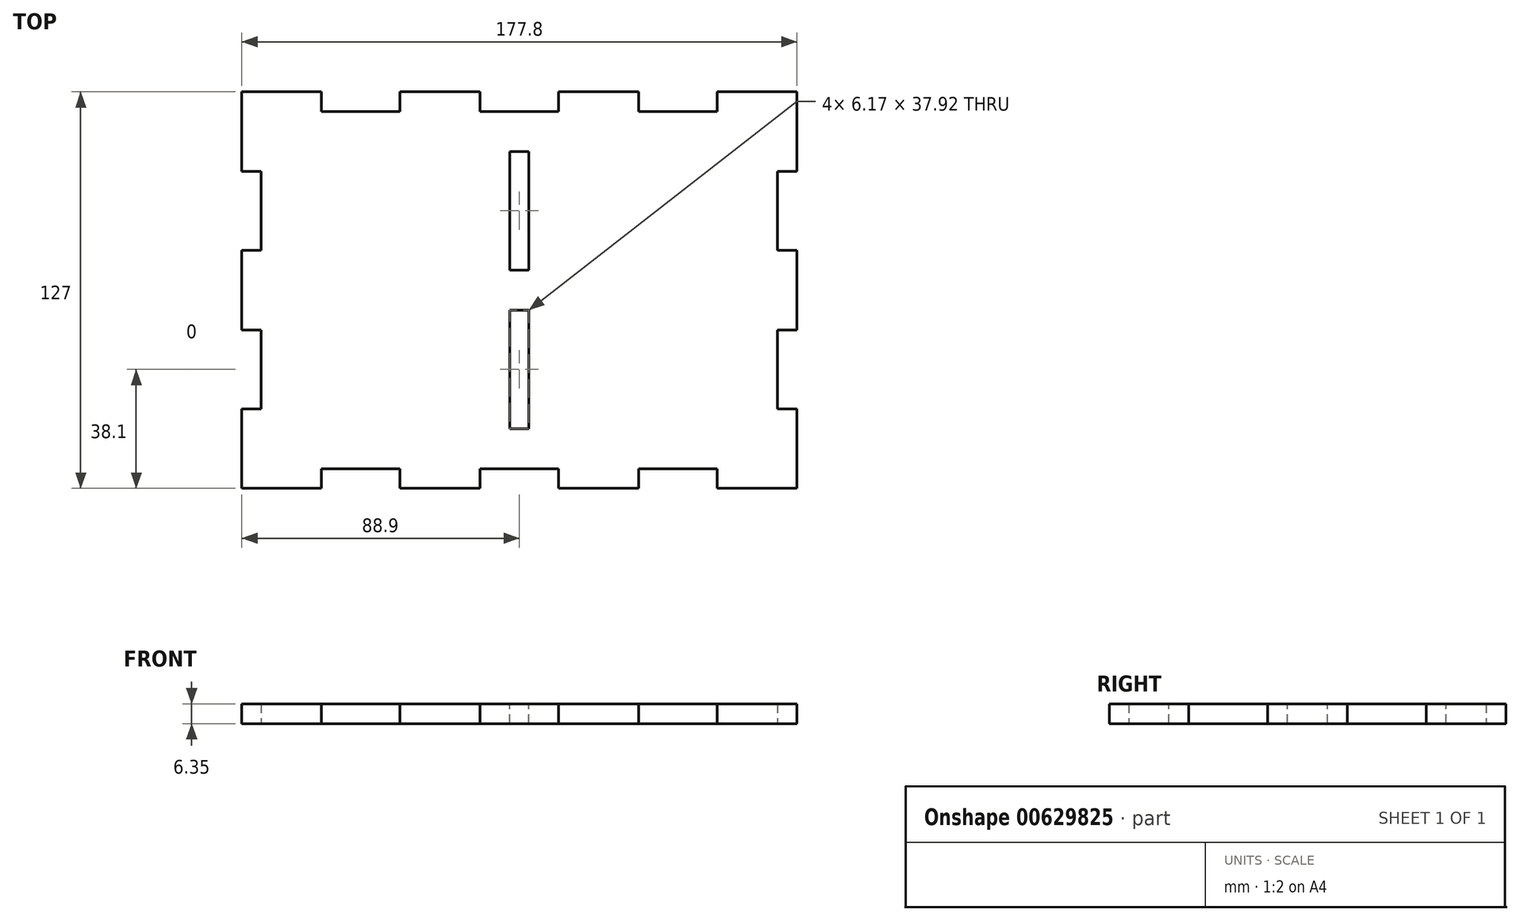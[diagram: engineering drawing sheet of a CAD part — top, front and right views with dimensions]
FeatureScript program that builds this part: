
annotation { "Feature Type Name" : "Feature", "Feature Type Description" : "" }
export const myFeature = defineFeature(function(context is Context, id is Id, definition is map)
    precondition{}
    {
        {
            var Q0;
            Q0=qCreatedBy(makeId("Top.planeOp"),FACE);
            var sketch = newSketch(context, id + "F0", { "sketchPlane" : qUnion([Q0])});
            skLineSegment(sketch, "E0.bottom", {"start": v(0, 0) * mm, "end": v(177.8, 0) * mm});
            skLineSegment(sketch, "E0.top", {"start": v(0, 127) * mm, "end": v(177.8, 127) * mm});
            skLineSegment(sketch, "E0.left", {"start": v(0, 0) * mm, "end": v(0, 127) * mm});
            skLineSegment(sketch, "E0.right", {"start": v(177.8, 0) * mm, "end": v(177.8, 127) * mm});
            skLineSegment(sketch, "E1.top", {"start": v(25.49, 6.26) * mm, "end": v(50.71, 6.26) * mm});
            skLineSegment(sketch, "E1.left", {"start": v(25.49, 0) * mm, "end": v(25.49, 6.26) * mm});
            skLineSegment(sketch, "E1.right", {"start": v(50.71, 0) * mm, "end": v(50.71, 6.26) * mm});
            skPoint(sketch, "E2", {"position": v(38.1, 6.26) * mm});
            skLineSegment(sketch, "E3.bottom", {"start": v(76.29, 0) * mm, "end": v(101.51, 0) * mm});
            skLineSegment(sketch, "E3.top", {"start": v(76.29, 6.26) * mm, "end": v(101.51, 6.26) * mm});
            skLineSegment(sketch, "E3.left", {"start": v(76.29, 0) * mm, "end": v(76.29, 6.26) * mm});
            skLineSegment(sketch, "E3.right", {"start": v(101.51, 0) * mm, "end": v(101.51, 6.26) * mm});
            skPoint(sketch, "E4", {"position": v(88.9, 6.26) * mm});
            skLineSegment(sketch, "E5.bottom", {"start": v(127.09, 0) * mm, "end": v(152.31, 0) * mm});
            skLineSegment(sketch, "E5.top", {"start": v(127.09, 6.26) * mm, "end": v(152.31, 6.26) * mm});
            skLineSegment(sketch, "E5.left", {"start": v(127.09, 0) * mm, "end": v(127.09, 6.26) * mm});
            skLineSegment(sketch, "E5.right", {"start": v(152.31, 0) * mm, "end": v(152.31, 6.26) * mm});
            skPoint(sketch, "E6", {"position": v(139.7, 6.26) * mm});
            skLineSegment(sketch, "E7.bottom", {"start": v(177.8, 25.49) * mm, "end": v(171.54, 25.49) * mm});
            skLineSegment(sketch, "E7.top", {"start": v(177.8, 50.71) * mm, "end": v(171.54, 50.71) * mm});
            skLineSegment(sketch, "E7.left", {"start": v(177.8, 25.49) * mm, "end": v(177.8, 50.71) * mm});
            skLineSegment(sketch, "E7.right", {"start": v(171.54, 25.49) * mm, "end": v(171.54, 50.71) * mm});
            skPoint(sketch, "E8", {"position": v(171.54, 38.1) * mm});
            skPoint(sketch, "E9", {"position": v(0, 63.5) * mm});
            skPoint(sketch, "E10", {"position": v(177.8, 63.5) * mm});
            skLineSegment(sketch, "E11", {"start": v(0, 63.5) * mm, "end": v(177.8, 63.5) * mm, "construction": true});
            skLineSegment(sketch, "E12.MirrorCS", {"start": v(25.49, 120.74) * mm, "end": v(50.71, 120.74) * mm});
            skLineSegment(sketch, "E13.MirrorCS", {"start": v(127.09, 120.74) * mm, "end": v(152.31, 120.74) * mm});
            skLineSegment(sketch, "E14.MirrorCS", {"start": v(50.71, 127) * mm, "end": v(50.71, 120.74) * mm});
            skLineSegment(sketch, "E15.MirrorCS", {"start": v(101.51, 127) * mm, "end": v(101.51, 120.74) * mm});
            skLineSegment(sketch, "E16.MirrorCS", {"start": v(76.29, 127) * mm, "end": v(101.51, 127) * mm});
            skPoint(sketch, "E17.MirrorP", {"position": v(139.7, 120.74) * mm});
            skLineSegment(sketch, "E18.MirrorCS", {"start": v(152.31, 127) * mm, "end": v(152.31, 120.74) * mm});
            skLineSegment(sketch, "E19.MirrorCS", {"start": v(127.09, 127) * mm, "end": v(152.31, 127) * mm});
            skLineSegment(sketch, "E20.MirrorCS", {"start": v(25.49, 127) * mm, "end": v(25.49, 120.74) * mm});
            skPoint(sketch, "E21.MirrorP", {"position": v(88.9, 120.74) * mm});
            skLineSegment(sketch, "E22.MirrorCS", {"start": v(127.09, 127) * mm, "end": v(127.09, 120.74) * mm});
            skLineSegment(sketch, "E23.MirrorCS", {"start": v(76.29, 120.74) * mm, "end": v(101.51, 120.74) * mm});
            skLineSegment(sketch, "E24.MirrorCS", {"start": v(76.29, 127) * mm, "end": v(76.29, 120.74) * mm});
            skPoint(sketch, "E25.MirrorP", {"position": v(38.1, 120.74) * mm});
            skLineSegment(sketch, "E26.MirrorCS", {"start": v(171.54, 101.51) * mm, "end": v(171.54, 76.29) * mm});
            skLineSegment(sketch, "E27.MirrorCS", {"start": v(177.8, 101.51) * mm, "end": v(177.8, 76.29) * mm});
            skLineSegment(sketch, "E28.MirrorCS", {"start": v(177.8, 101.51) * mm, "end": v(171.54, 101.51) * mm});
            skLineSegment(sketch, "E29.MirrorCS", {"start": v(177.8, 76.29) * mm, "end": v(171.54, 76.29) * mm});
            skPoint(sketch, "E30.MirrorP", {"position": v(171.54, 88.9) * mm});
            skPoint(sketch, "E31", {"position": v(88.9, 127) * mm});
            skPoint(sketch, "E32", {"position": v(88.9, 0) * mm});
            skLineSegment(sketch, "E33", {"start": v(88.9, 127) * mm, "end": v(88.9, 0) * mm, "construction": true});
            skLineSegment(sketch, "E34.MirrorCS", {"start": v(0, 76.29) * mm, "end": v(6.26, 76.29) * mm});
            skPoint(sketch, "E35.MirrorP", {"position": v(6.26, 88.9) * mm});
            skLineSegment(sketch, "E36.MirrorCS", {"start": v(6.26, 25.49) * mm, "end": v(6.26, 50.71) * mm});
            skLineSegment(sketch, "E37.MirrorCS", {"start": v(6.26, 101.51) * mm, "end": v(6.26, 76.29) * mm});
            skLineSegment(sketch, "E38.MirrorCS", {"start": v(0, 101.51) * mm, "end": v(6.26, 101.51) * mm});
            skLineSegment(sketch, "E39.MirrorCS", {"start": v(0, 25.49) * mm, "end": v(0, 50.71) * mm});
            skPoint(sketch, "E40.MirrorP", {"position": v(6.26, 38.1) * mm});
            skLineSegment(sketch, "E41.MirrorCS", {"start": v(0, 25.49) * mm, "end": v(6.26, 25.49) * mm});
            skLineSegment(sketch, "E42.MirrorCS", {"start": v(0, 101.51) * mm, "end": v(0, 76.29) * mm});
            skLineSegment(sketch, "E43.MirrorCS", {"start": v(0, 50.71) * mm, "end": v(6.26, 50.71) * mm});
            skSolve(sketch);
        }
        {
            var Q0;
            Q0=makeQuery(id+"F0.imprint","IMPRINT",FACE,{"disambiguationData":[TD([[makeQuery(id+"F0.imprint","IMPRINT",EDGE,{"derivedFrom":sQuery(id+"F0.wireOp",EDGE,"E1.top")}),1.0]])]});
            extrude(context, id + "F1", {"entities" : qUnion([Q0]), "depth" : 6.35 * mm, "offsetDistance" : 25.4 * mm});
        }
        {
            var Q0;
            Q0=makeQuery(id+"F1.opExtrude","CAP_FACE",FACE,{"disambiguationData":[OSD([sQuery(id+"F0.wireOp",EDGE,"E0.bottom"),sQuery(id+"F0.wireOp",EDGE,"E0.top"),sQuery(id+"F0.wireOp",EDGE,"E0.left"),sQuery(id+"F0.wireOp",EDGE,"E0.right"),sQuery(id+"F0.wireOp",EDGE,"E1.top"),sQuery(id+"F0.wireOp",EDGE,"E1.left"),sQuery(id+"F0.wireOp",EDGE,"E1.right"),sQuery(id+"F0.wireOp",EDGE,"E3.top"),sQuery(id+"F0.wireOp",EDGE,"E3.left"),sQuery(id+"F0.wireOp",EDGE,"E3.right"),sQuery(id+"F0.wireOp",EDGE,"E5.top"),sQuery(id+"F0.wireOp",EDGE,"E5.left"),sQuery(id+"F0.wireOp",EDGE,"E5.right"),sQuery(id+"F0.wireOp",EDGE,"E7.bottom"),sQuery(id+"F0.wireOp",EDGE,"E7.top"),sQuery(id+"F0.wireOp",EDGE,"E7.right"),sQuery(id+"F0.wireOp",EDGE,"E12.MirrorCS"),sQuery(id+"F0.wireOp",EDGE,"E13.MirrorCS"),sQuery(id+"F0.wireOp",EDGE,"E14.MirrorCS"),sQuery(id+"F0.wireOp",EDGE,"E15.MirrorCS"),sQuery(id+"F0.wireOp",EDGE,"E18.MirrorCS"),sQuery(id+"F0.wireOp",EDGE,"E20.MirrorCS"),sQuery(id+"F0.wireOp",EDGE,"E22.MirrorCS"),sQuery(id+"F0.wireOp",EDGE,"E23.MirrorCS"),sQuery(id+"F0.wireOp",EDGE,"E24.MirrorCS"),sQuery(id+"F0.wireOp",EDGE,"E26.MirrorCS"),sQuery(id+"F0.wireOp",EDGE,"E28.MirrorCS"),sQuery(id+"F0.wireOp",EDGE,"E29.MirrorCS"),sQuery(id+"F0.wireOp",EDGE,"E34.MirrorCS"),sQuery(id+"F0.wireOp",EDGE,"E36.MirrorCS"),sQuery(id+"F0.wireOp",EDGE,"E37.MirrorCS"),sQuery(id+"F0.wireOp",EDGE,"E38.MirrorCS"),sQuery(id+"F0.wireOp",EDGE,"E41.MirrorCS"),sQuery(id+"F0.wireOp",EDGE,"E43.MirrorCS")])],"isStart":false});
            var sketch = newSketch(context, id + "F2", { "sketchPlane" : qUnion([Q0])});
            skLineSegment(sketch, "E44.bottom", {"start": v(85.81, 107.86) * mm, "end": v(91.99, 107.86) * mm});
            skLineSegment(sketch, "E44.top", {"start": v(85.81, 69.94) * mm, "end": v(91.99, 69.94) * mm});
            skLineSegment(sketch, "E44.left", {"start": v(85.81, 107.86) * mm, "end": v(85.81, 69.94) * mm});
            skLineSegment(sketch, "E44.right", {"start": v(91.99, 107.86) * mm, "end": v(91.99, 69.94) * mm});
            skLineSegment(sketch, "E45.bottom", {"start": v(85.81, 57.06) * mm, "end": v(91.99, 57.06) * mm});
            skLineSegment(sketch, "E45.top", {"start": v(85.81, 19.14) * mm, "end": v(91.99, 19.14) * mm});
            skLineSegment(sketch, "E45.left", {"start": v(85.81, 57.06) * mm, "end": v(85.81, 19.14) * mm});
            skLineSegment(sketch, "E45.right", {"start": v(91.99, 57.06) * mm, "end": v(91.99, 19.14) * mm});
            skPoint(sketch, "E46", {"position": v(88.9, 19.14) * mm});
            skPoint(sketch, "E47", {"position": v(91.99, 38.1) * mm});
            skPoint(sketch, "E48", {"position": v(88.9, 69.94) * mm});
            skPoint(sketch, "E49", {"position": v(91.99, 88.9) * mm});
            skSolve(sketch);
        }
        {
            var Q0;
            Q0 = qSketchRegion(id + "F2", true);
            extrude(context, id + "F3", {"entities" : qUnion([Q0]), "operationType" : NewBodyOperationType.REMOVE, "endBound" : BoundingType.THROUGH_ALL, "oppositeDirection" : true, "depth" : 25.4 * mm, "offsetDistance" : 25.4 * mm});
        }
    });
